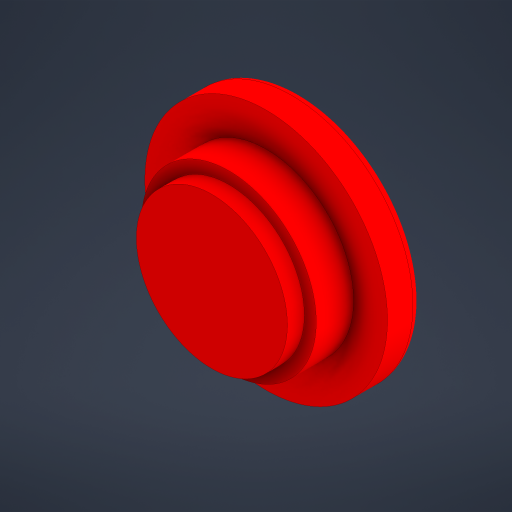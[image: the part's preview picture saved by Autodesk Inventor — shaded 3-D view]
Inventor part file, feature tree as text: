
AUTODESK INVENTOR PART (.ipt)
format: ipt  version: 2023.4 (Build 274418000, 418)  size: 237,568 bytes
history: native  units: mm
features: extrude x4, sketch x2, fillet x1, chamfer x1
ambient origin geometry x8: Origin, YZ Plane, XZ Plane, XY Plane, X Axis, Y Axis, Z Axis, Center Point
bodies: Solid1 (feature_tree)
feature tree (8):
  sketch  "Sketch1"  dims[d0=22.25mm d1=25.75mm]
  extrude  "Extrusion1"  Depth=25.75mm
  extrude  "Extrusion2"  Depth=5.0mm TaperAngle=0.0deg
  extrude  "Extrusion3"  Depth=5.5mm TaperAngle=0.0deg
  fillet  "Fillet1"  Radius=2.5mm
  extrude  "Extrusion4"  Depth=1.25mm
  chamfer  "Chamfer1"  Distance=25.0mm
  sketch  "Sketch2"  dims[d2=5.0mm d3=5.0mm d4=0.0mm d5=5.5mm d6=0.0mm d7=2.5mm d8=0.0mm d9=1.25mm d10=25.0mm d11=25.0mm d12=0.25mm d13=0.0mm d14=0.25mm d15=2.0mm d16=45.0deg]
